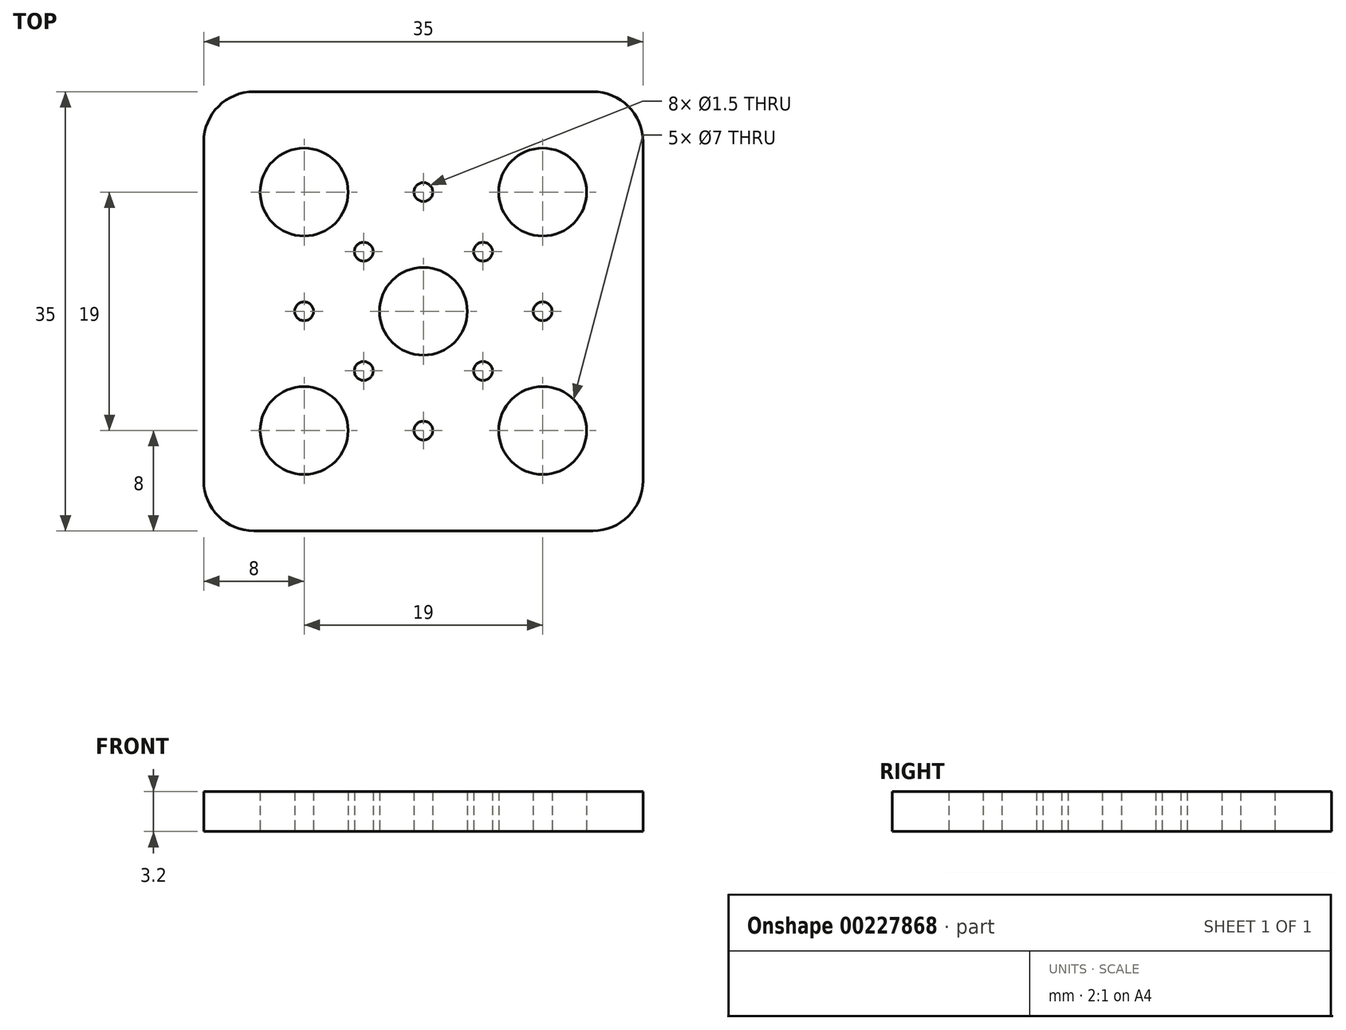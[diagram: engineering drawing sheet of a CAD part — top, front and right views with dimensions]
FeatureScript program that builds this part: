
annotation { "Feature Type Name" : "Feature", "Feature Type Description" : "" }
export const myFeature = defineFeature(function(context is Context, id is Id, definition is map)
    precondition{}
    {
        {
            var Q0;
            Q0=qCreatedBy(makeId("Top.planeOp"),FACE);
            var sketch = newSketch(context, id + "F0", { "sketchPlane" : qUnion([Q0])});
            skCircle(sketch, "E0", {"center": v(0, 0) * mm, "radius": 0.75 * mm});
            skCircle(sketch, "E1.0.1.0", {"center": v(0, 9.5) * mm, "radius": 0.75 * mm});
            skCircle(sketch, "E1.0.2.0", {"center": v(0, 19) * mm, "radius": 0.75 * mm});
            skCircle(sketch, "E1.1.0.0", {"center": v(9.5, 0) * mm, "radius": 0.75 * mm});
            skCircle(sketch, "E1.1.1.0", {"center": v(9.5, 9.5) * mm, "radius": 0.75 * mm});
            skCircle(sketch, "E1.1.2.0", {"center": v(9.5, 19) * mm, "radius": 0.75 * mm});
            skCircle(sketch, "E1.2.0.0", {"center": v(19, 0) * mm, "radius": 0.75 * mm});
            skCircle(sketch, "E1.2.1.0", {"center": v(19, 9.5) * mm, "radius": 0.75 * mm});
            skCircle(sketch, "E1.2.2.0", {"center": v(19, 19) * mm, "radius": 0.75 * mm});
            skLineSegment(sketch, "E1.direction1", {"start": v(0, 0) * mm, "end": v(9.5, 0) * mm, "construction": true});
            skLineSegment(sketch, "E1.direction2", {"start": v(0, 0) * mm, "end": v(0, 9.5) * mm, "construction": true});
            skLineSegment(sketch, "E2.bottom", {"start": v(23, 27) * mm, "end": v(-4, 27) * mm});
            skLineSegment(sketch, "E2.top", {"start": v(23, -8) * mm, "end": v(-4, -8) * mm});
            skLineSegment(sketch, "E2.left", {"start": v(27, 23) * mm, "end": v(27, -4) * mm});
            skLineSegment(sketch, "E2.right", {"start": v(-8, 23) * mm, "end": v(-8, -4) * mm});
            skPoint(sketch, "E3.visualSharp", {"position": v(-8, 27) * mm});
            skArc(sketch, "E3.filletArc", {"start": v(-4, 27) * mm, "mid": v(-6.83, 25.83) * mm, "end": v(-8, 23) * mm});
            skPoint(sketch, "E4.visualSharp", {"position": v(27, 27) * mm});
            skArc(sketch, "E4.filletArc", {"start": v(27, 23) * mm, "mid": v(25.83, 25.83) * mm, "end": v(23, 27) * mm});
            skPoint(sketch, "E5.visualSharp", {"position": v(27, -8) * mm});
            skArc(sketch, "E5.filletArc", {"start": v(23, -8) * mm, "mid": v(25.83, -6.83) * mm, "end": v(27, -4) * mm});
            skPoint(sketch, "E6.visualSharp", {"position": v(-8, -8) * mm});
            skArc(sketch, "E6.filletArc", {"start": v(-8, -4) * mm, "mid": v(-6.83, -6.83) * mm, "end": v(-4, -8) * mm});
            skLineSegment(sketch, "E7", {"start": v(9.5, 9.5) * mm, "end": v(0, 0) * mm, "construction": true});
            skCircle(sketch, "E8.1.1.0", {"center": v(4.75, 4.75) * mm, "radius": 0.75 * mm});
            skLineSegment(sketch, "E8.direction1", {"start": v(-4.75, -4.75) * mm, "end": v(4.75, -4.75) * mm, "construction": true});
            skLineSegment(sketch, "E8.direction2", {"start": v(-4.75, -4.75) * mm, "end": v(-4.75, 4.75) * mm, "construction": true});
            skCircle(sketch, "E9.0.2.1", {"center": v(14.25, 4.75) * mm, "radius": 0.75 * mm});
            skCircle(sketch, "E10.0.1.2", {"center": v(4.75, 14.25) * mm, "radius": 0.75 * mm});
            skCircle(sketch, "E10.0.2.2", {"center": v(14.25, 14.25) * mm, "radius": 0.75 * mm});
            skCircle(sketch, "E11", {"center": v(0, 0) * mm, "radius": 3.5 * mm});
            skCircle(sketch, "E12", {"center": v(9.5, 9.5) * mm, "radius": 3.5 * mm});
            skCircle(sketch, "E13", {"center": v(19, 0) * mm, "radius": 3.5 * mm});
            skCircle(sketch, "E14", {"center": v(19, 19) * mm, "radius": 3.5 * mm});
            skCircle(sketch, "E15", {"center": v(0, 19) * mm, "radius": 3.5 * mm});
            skSolve(sketch);
        }
        {
            var Q0;
            Q0=makeQuery(id+"F0.imprint","IMPRINT",FACE,{"disambiguationData":[TD([[makeQuery(id+"F0.imprint","IMPRINT",EDGE,{"derivedFrom":sQuery(id+"F0.wireOp",EDGE,"E1.0.1.0")}),-1.0]])]});
            extrude(context, id + "F1", {"entities" : qUnion([Q0]), "depth" : 3.2 * mm, "offsetDistance" : 25 * mm});
        }
    });
